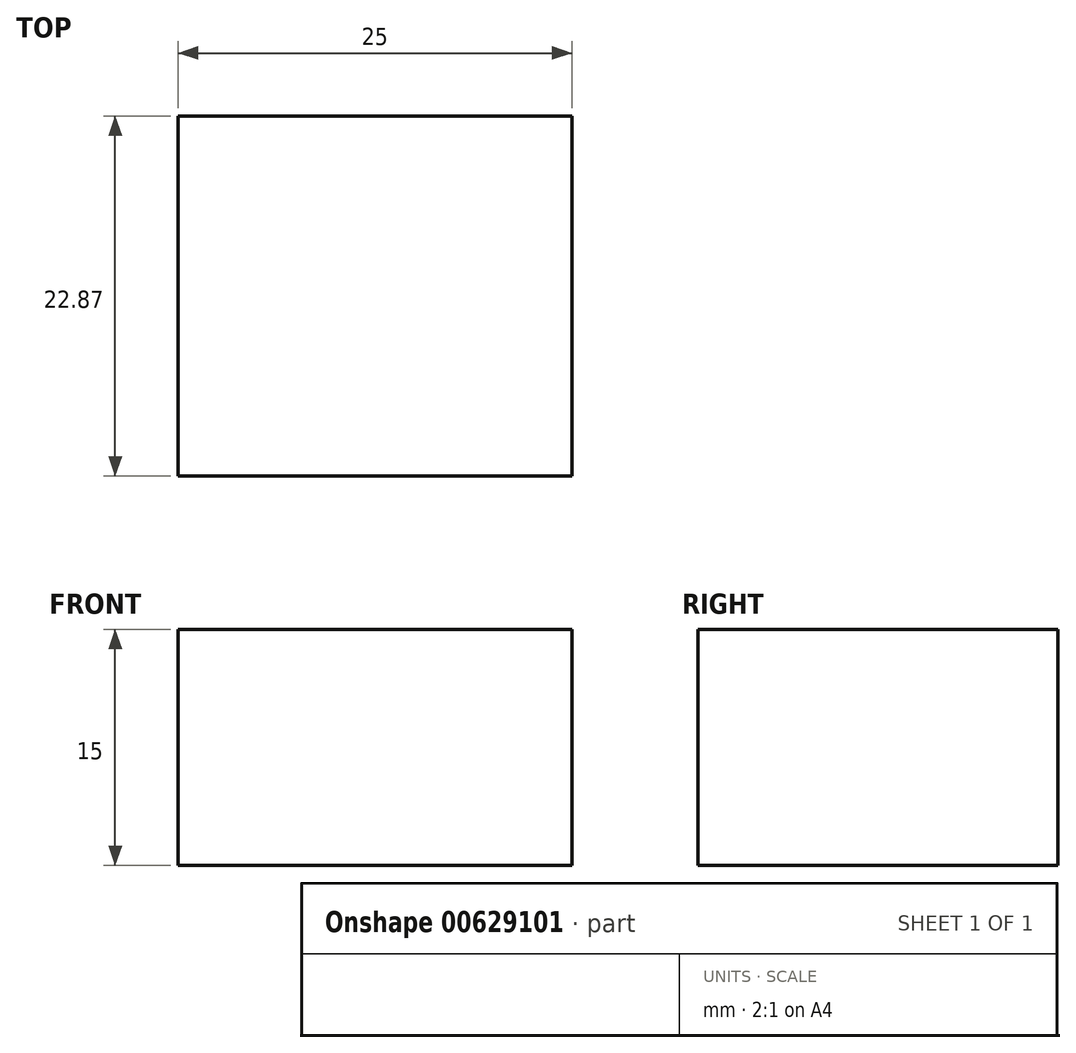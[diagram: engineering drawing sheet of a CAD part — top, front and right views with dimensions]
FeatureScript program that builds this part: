
annotation { "Feature Type Name" : "Feature", "Feature Type Description" : "" }
export const myFeature = defineFeature(function(context is Context, id is Id, definition is map)
    precondition{}
    {
        {
            var Q0;
            Q0=qCreatedBy(makeId("Top.planeOp"),FACE);
            var sketch = newSketch(context, id + "F0", { "sketchPlane" : qUnion([Q0])});
            skLineSegment(sketch, "E0.bottom", {"start": v(0, 0) * mm, "end": v(25, 0) * mm});
            skLineSegment(sketch, "E0.top", {"start": v(0, 22.87) * mm, "end": v(25, 22.87) * mm});
            skLineSegment(sketch, "E0.left", {"start": v(0, 0) * mm, "end": v(0, 22.87) * mm});
            skLineSegment(sketch, "E0.right", {"start": v(25, 0) * mm, "end": v(25, 22.87) * mm});
            skSolve(sketch);
        }
        {
            var Q0;
            Q0 = qSketchRegion(id + "F0", true);
            extrude(context, id + "F1", {"entities" : qUnion([Q0]), "depth" : 15 * mm, "offsetDistance" : 25 * mm});
        }
    });
